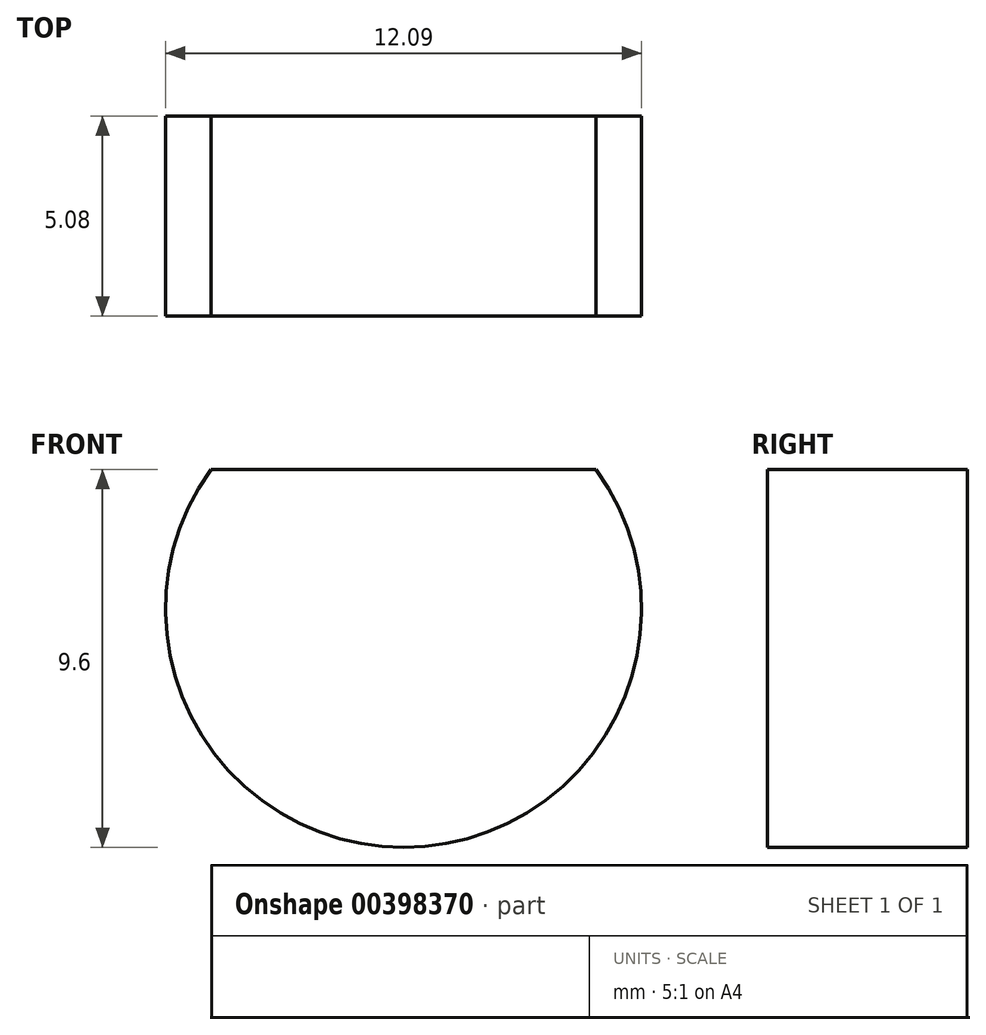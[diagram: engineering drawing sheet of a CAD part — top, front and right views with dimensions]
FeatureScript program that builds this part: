
annotation { "Feature Type Name" : "Feature", "Feature Type Description" : "" }
export const myFeature = defineFeature(function(context is Context, id is Id, definition is map)
    precondition{}
    {
        {
            var Q0;
            Q0=qCreatedBy(makeId("Front.planeOp"),FACE);
            var sketch = newSketch(context, id + "F0", { "sketchPlane" : qUnion([Q0])});
            skLineSegment(sketch, "E0", {"start": v(-48.93, 0) * mm, "end": v(-39.14, 0) * mm});
            skArc(sketch, "E1", {"start": v(-48.93, 0) * mm, "mid": v(-44.03, -9.6) * mm, "end": v(-39.14, 0) * mm});
            skSolve(sketch);
        }
        {
            var Q0;
            Q0=makeQuery(id+"F0.imprint","IMPRINT",FACE,{"disambiguationData":[TD([[makeQuery(id+"F0.imprint","IMPRINT",EDGE,{"derivedFrom":sQuery(id+"F0.wireOp",EDGE,"E0")}),-1.0]])]});
            extrude(context, id + "F1", {"entities" : qUnion([Q0]), "depth" : 5.08 * mm});
        }
    });
